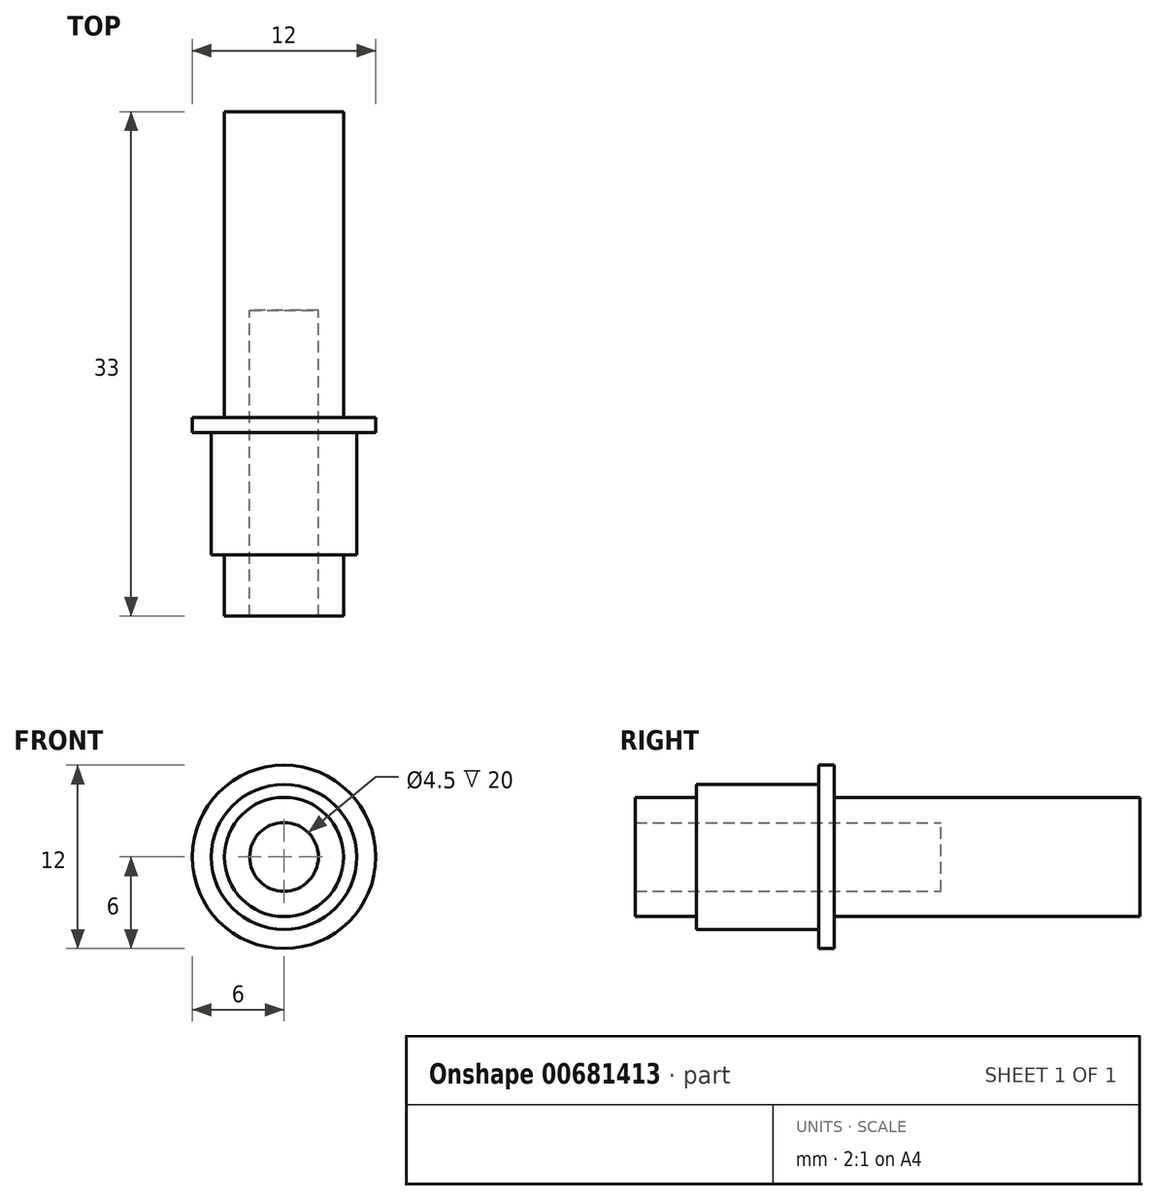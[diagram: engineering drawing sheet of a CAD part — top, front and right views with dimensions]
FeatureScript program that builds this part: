
annotation { "Feature Type Name" : "Feature", "Feature Type Description" : "" }
export const myFeature = defineFeature(function(context is Context, id is Id, definition is map)
    precondition{}
    {
        {
            var Q0;
            Q0=qCreatedBy(makeId("Front.planeOp"),FACE);
            var sketch = newSketch(context, id + "F0", { "sketchPlane" : qUnion([Q0])});
            skCircle(sketch, "E0", {"center": v(0, 0) * mm, "radius": 3.9 * mm});
            skCircle(sketch, "E1", {"center": v(0, 0) * mm, "radius": 6 * mm});
            skCircle(sketch, "E2", {"center": v(0, 0) * mm, "radius": 2.25 * mm});
            skCircle(sketch, "E3", {"center": v(0, 0) * mm, "radius": 4.75 * mm});
            skSolve(sketch);
        }
        {
            var Q0;
            Q0=makeQuery(id+"F0.imprint","IMPRINT",FACE,{"disambiguationData":[TD([[makeQuery(id+"F0.imprint","IMPRINT",EDGE,{"derivedFrom":sQuery(id+"F0.wireOp",EDGE,"E0")}),1.0]])]});
            extrude(context, id + "F1", {"entities" : qUnion([Q0]), "depth" : 13 * mm, "offsetDistance" : 25 * mm});
        }
        {
            var Q0;
            Q0=qCreatedBy(makeId("Front.planeOp"),FACE);
            cPlane(context, id + "F2", {"entities" : qUnion([Q0]), "cplaneType" : CPlaneType.OFFSET, "offset" : 9 * mm, "width" : 150 * mm, "height" : 150 * mm});
        }
        {
            var Q0;
            Q0=makeQuery(id+"F0.imprint","IMPRINT",FACE,{"disambiguationData":[TD([[makeQuery(id+"F0.imprint","IMPRINT",EDGE,{"derivedFrom":sQuery(id+"F0.wireOp",EDGE,"E0")}),-1.0]])]});
            extrude(context, id + "F3", {"entities" : qUnion([Q0]), "operationType" : NewBodyOperationType.ADD, "depth" : 9 * mm, "offsetDistance" : 25 * mm});
        }
        {
            var Q0;
            Q0=makeQuery(id+"F0.imprint","IMPRINT",FACE,{"disambiguationData":[TD([[makeQuery(id+"F0.imprint","IMPRINT",EDGE,{"derivedFrom":sQuery(id+"F0.wireOp",EDGE,"E1")}),1.0]])]});
            extrude(context, id + "F4", {"entities" : qUnion([Q0]), "operationType" : NewBodyOperationType.ADD, "depth" : 1 * mm, "offsetDistance" : 25 * mm});
        }
        {
            var Q0;
            Q0=makeQuery(id+"F0.imprint","IMPRINT",FACE,{"disambiguationData":[TD([[makeQuery(id+"F0.imprint","IMPRINT",EDGE,{"derivedFrom":sQuery(id+"F0.wireOp",EDGE,"E2")}),1.0]])]});
            var Q1;
            Q1=makeQuery(id+"F0.imprint","IMPRINT",FACE,{"disambiguationData":[TD([[makeQuery(id+"F0.imprint","IMPRINT",EDGE,{"derivedFrom":sQuery(id+"F0.wireOp",EDGE,"E0")}),1.0]])]});
            extrude(context, id + "F5", {"entities" : qUnion([Q0, Q1]), "operationType" : NewBodyOperationType.ADD, "oppositeDirection" : true, "depth" : 20 * mm, "offsetDistance" : 25 * mm});
        }
        {
            var Q0;
            Q0=makeQuery(id+"F0.imprint","IMPRINT",FACE,{"disambiguationData":[TD([[makeQuery(id+"F0.imprint","IMPRINT",EDGE,{"derivedFrom":sQuery(id+"F0.wireOp",EDGE,"E2")}),1.0]])]});
            extrude(context, id + "F6", {"entities" : qUnion([Q0]), "operationType" : NewBodyOperationType.REMOVE, "oppositeDirection" : true, "depth" : 7 * mm, "offsetDistance" : 25 * mm});
        }
    });
